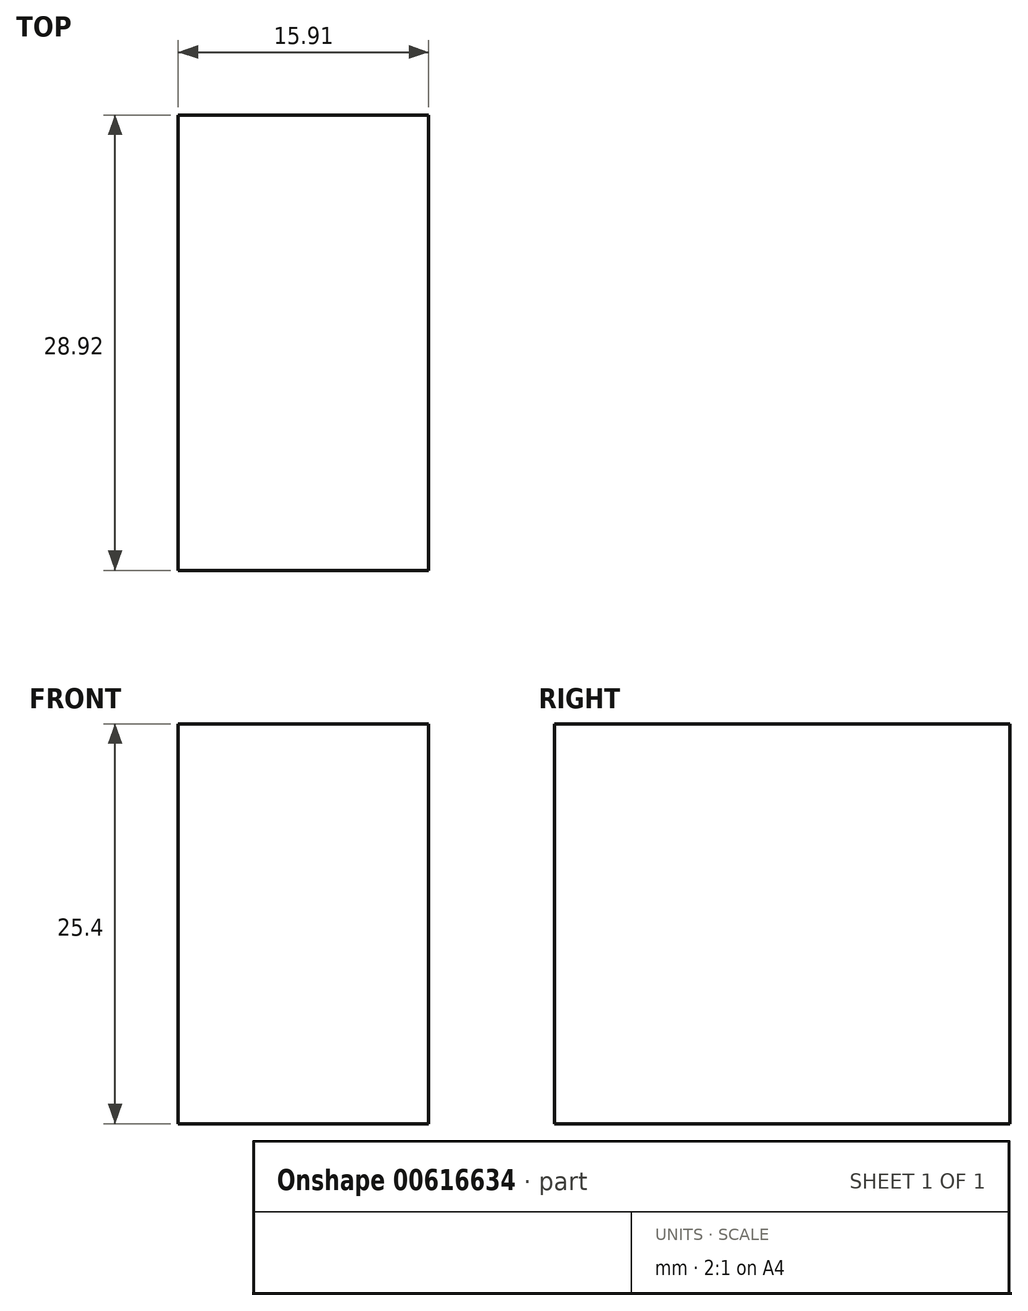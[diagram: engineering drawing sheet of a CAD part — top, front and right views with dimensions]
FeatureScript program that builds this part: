
annotation { "Feature Type Name" : "Feature", "Feature Type Description" : "" }
export const myFeature = defineFeature(function(context is Context, id is Id, definition is map)
    precondition{}
    {
        {
            var Q0;
            Q0=qCreatedBy(makeId("Top.planeOp"),FACE);
            var sketch = newSketch(context, id + "F0", { "sketchPlane" : qUnion([Q0])});
            skLineSegment(sketch, "E0.bottom", {"start": v(70.14, 51.77) * mm, "end": v(86.05, 51.77) * mm});
            skLineSegment(sketch, "E0.top", {"start": v(70.14, 22.85) * mm, "end": v(86.05, 22.85) * mm});
            skLineSegment(sketch, "E0.left", {"start": v(70.14, 51.77) * mm, "end": v(70.14, 22.85) * mm});
            skLineSegment(sketch, "E0.right", {"start": v(86.05, 51.77) * mm, "end": v(86.05, 22.85) * mm});
            skArc(sketch, "E1", {"start": v(70.14, 22.85) * mm, "mid": v(66.75, 9.95) * mm, "end": v(57.46, 0.39) * mm});
            skArc(sketch, "E2", {"start": v(76.2, -27.31) * mm, "mid": v(88.2, -3.82) * mm, "end": v(87.2, 22.55) * mm});
            skArc(sketch, "E3", {"start": v(31.26, 0.54) * mm, "mid": v(19.02, 8.84) * mm, "end": v(5.5, 14.85) * mm});
            skArc(sketch, "E4", {"start": v(13.67, -13.35) * mm, "mid": v(20.92, -22.04) * mm, "end": v(31.06, -27.09) * mm});
            skSolve(sketch);
        }
        {
            var Q0;
            Q0 = qSketchRegion(id + "F0", true);
            extrude(context, id + "F1", {"entities" : qUnion([Q0]), "depth" : 25.4 * mm, "offsetDistance" : 25.4 * mm});
        }
    });
